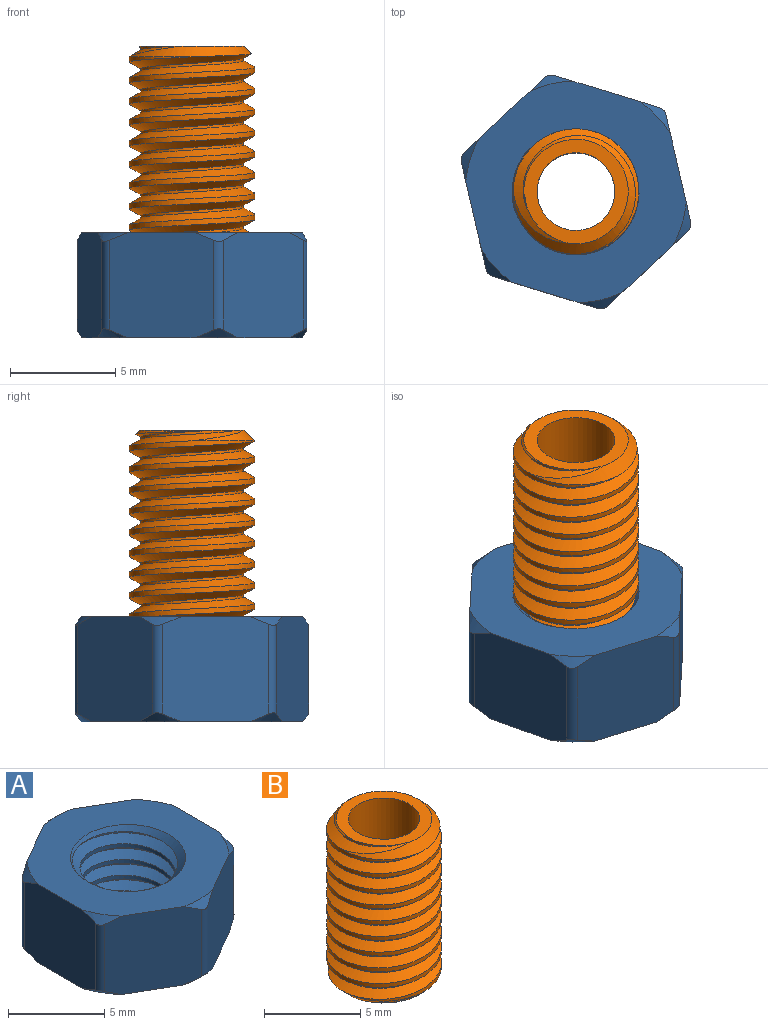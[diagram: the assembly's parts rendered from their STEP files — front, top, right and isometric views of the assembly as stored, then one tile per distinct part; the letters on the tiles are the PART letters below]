
ASSEMBLY  parts=2 mates=1
PART A: 32 faces, bbox 10.7x11.4x5.8 mm
  f0: cylinder r=2.5mm len=5mm, axis (0,0,1), area 15.9mm2, adj f9,f10,f30,f31
  f1: plane 5.06x4.56mm, normal (0.5,0.87,0), area 25.4mm2, adj f7,f8,f11,f14,f21,f22,f23,f28
  f2: plane 5.06x4.56mm, normal (-0.5,0.87,0), area 25.4mm2, adj f7,f8,f19,f20,f21,f22,f23,f24
  f3: plane 5.26x5.06mm, normal (-1,0,0), area 25.4mm2, adj f7,f8,f17,f18,f19,f20,f24,f25
  f4: plane 5.06x4.56mm, normal (-0.5,-0.87,0), area 25.4mm2, adj f7,f8,f15,f16,f17,f18,f25,f26
  f5: plane 5.06x4.56mm, normal (0.5,-0.87,0), area 25.4mm2, adj f7,f8,f12,f13,f15,f16,f26,f27
  f6: plane 5.26x5.06mm, normal (1,0,0), area 25.4mm2, adj f7,f8,f11,f12,f13,f14,f27,f28
  f7: plane 10.55x10mm, normal (0,0,1), area 55.3mm2, adj f1,f2,f3,f4,f5,f6,f10,f13
  f8: plane 10.55x10mm, normal (0,0,-1), area 55.3mm2, adj f1,f2,f3,f4,f5,f6,f9,f11
  f9: cone r=3mm half-angle=45deg, axis (0,0,-1), area 6.7mm2, adj f0,f8,f30,f31
  f10: cone r=2.5mm half-angle=45deg, axis (0,0,1), area 6.7mm2, adj f0,f7,f30,f31
  f11: cone r=5.77mm half-angle=45deg, axis (0,0,1), area 0.7mm2, adj f1,f6,f8,f28
  f12: cone r=5.77mm half-angle=45deg, axis (0,0,1), area 0.7mm2, adj f5,f6,f8,f27
  f13: cone r=5.27mm half-angle=45deg, axis (0,0,-1), area 0.7mm2, adj f5,f6,f7,f27
  f14: cone r=5.27mm half-angle=45deg, axis (0,0,-1), area 0.7mm2, adj f1,f6,f7,f28
  f15: cone r=5.77mm half-angle=45deg, axis (0,0,1), area 0.7mm2, adj f4,f5,f8,f26
  f16: cone r=5.27mm half-angle=45deg, axis (0,0,-1), area 0.7mm2, adj f4,f5,f7,f26
  f17: cone r=5.77mm half-angle=45deg, axis (0,0,1), area 0.7mm2, adj f3,f4,f8,f25
  f18: cone r=5.27mm half-angle=45deg, axis (0,0,-1), area 0.7mm2, adj f3,f4,f7,f25
  f19: cone r=5.77mm half-angle=45deg, axis (0,0,1), area 0.7mm2, adj f2,f3,f8,f24
  f20: cone r=5.27mm half-angle=45deg, axis (0,0,-1), area 0.7mm2, adj f2,f3,f7,f24
  f21: cone r=5.77mm half-angle=45deg, axis (0,0,1), area 0.7mm2, adj f1,f2,f8,f23
  f22: cone r=5.27mm half-angle=45deg, axis (0,0,-1), area 0.7mm2, adj f1,f2,f7,f23
  f23: cylinder r=0.5mm len=4.28mm, axis (0,0,-1), area 2.2mm2, adj f1,f2,f21,f22
  f24: cylinder r=0.5mm len=4.28mm, axis (0,0,-1), area 2.2mm2, adj f2,f3,f19,f20
  f25: cylinder r=0.5mm len=4.28mm, axis (0,0,-1), area 2.2mm2, adj f3,f4,f17,f18
  f26: cylinder r=0.5mm len=4.28mm, axis (0,0,-1), area 2.2mm2, adj f4,f5,f15,f16
  f27: cylinder r=0.5mm len=4.28mm, axis (0,0,-1), area 2.2mm2, adj f5,f6,f12,f13
  f28: cylinder r=0.5mm len=4.28mm, axis (0,0,-1), area 2.2mm2, adj f1,f6,f11,f14
  f29: cylinder r=3.04mm len=6.08mm, axis (0,0,-1), area 11.5mm2, adj f7,f8,f30,f31
  f30: bspline ~7.02x6.08mm, area 49.6mm2, adj f0,f7,f8,f9,f10,f29
  f31: bspline ~7.02x6.08mm, area 49.6mm2, adj f0,f7,f8,f9,f10,f29
PART B: 9 faces, bbox 6x6.9x10.8 mm
  f0: cylinder r=2.99mm len=9mm, axis (0,0,-1), area 58.1mm2, adj f4,f5,f7,f8
  f1: cylinder r=1.85mm len=10mm, axis (0,0,-1), area 116.3mm2, adj f2,f3
  f2: plane 4.98x4.98mm, normal (0,0,1), area 8.6mm2, adj f1,f5,f6,f7,f8
  f3: plane 4.98x4.98mm, normal (0,0,-1), area 8.6mm2, adj f1,f4,f6,f7,f8
  f4: cone r=2.99mm half-angle=45deg, axis (0,0,1), area 6.4mm2, adj f0,f3,f7,f8
  f5: cone r=2.49mm half-angle=45deg, axis (0,0,-1), area 6.4mm2, adj f0,f2,f7,f8
  f6: cylinder r=2.45mm len=10mm, axis (0,0,-1), area 21.4mm2, adj f2,f3,f7,f8
  f7: bspline ~10.48x6.9mm, area 101.7mm2, adj f0,f2,f3,f4,f5,f6
  f8: bspline ~10.48x6.9mm, area 102mm2, adj f0,f2,f3,f4,f5,f6
PLACE A rot(axis=(0,0,-1),47deg) t=(0,0,-13.87)mm
PLACE B t=(0,0,-10)mm
MATE cylindrical A.f0 <-> B.f0  axis (0,0,1) through (0,0,-8.87)mm
